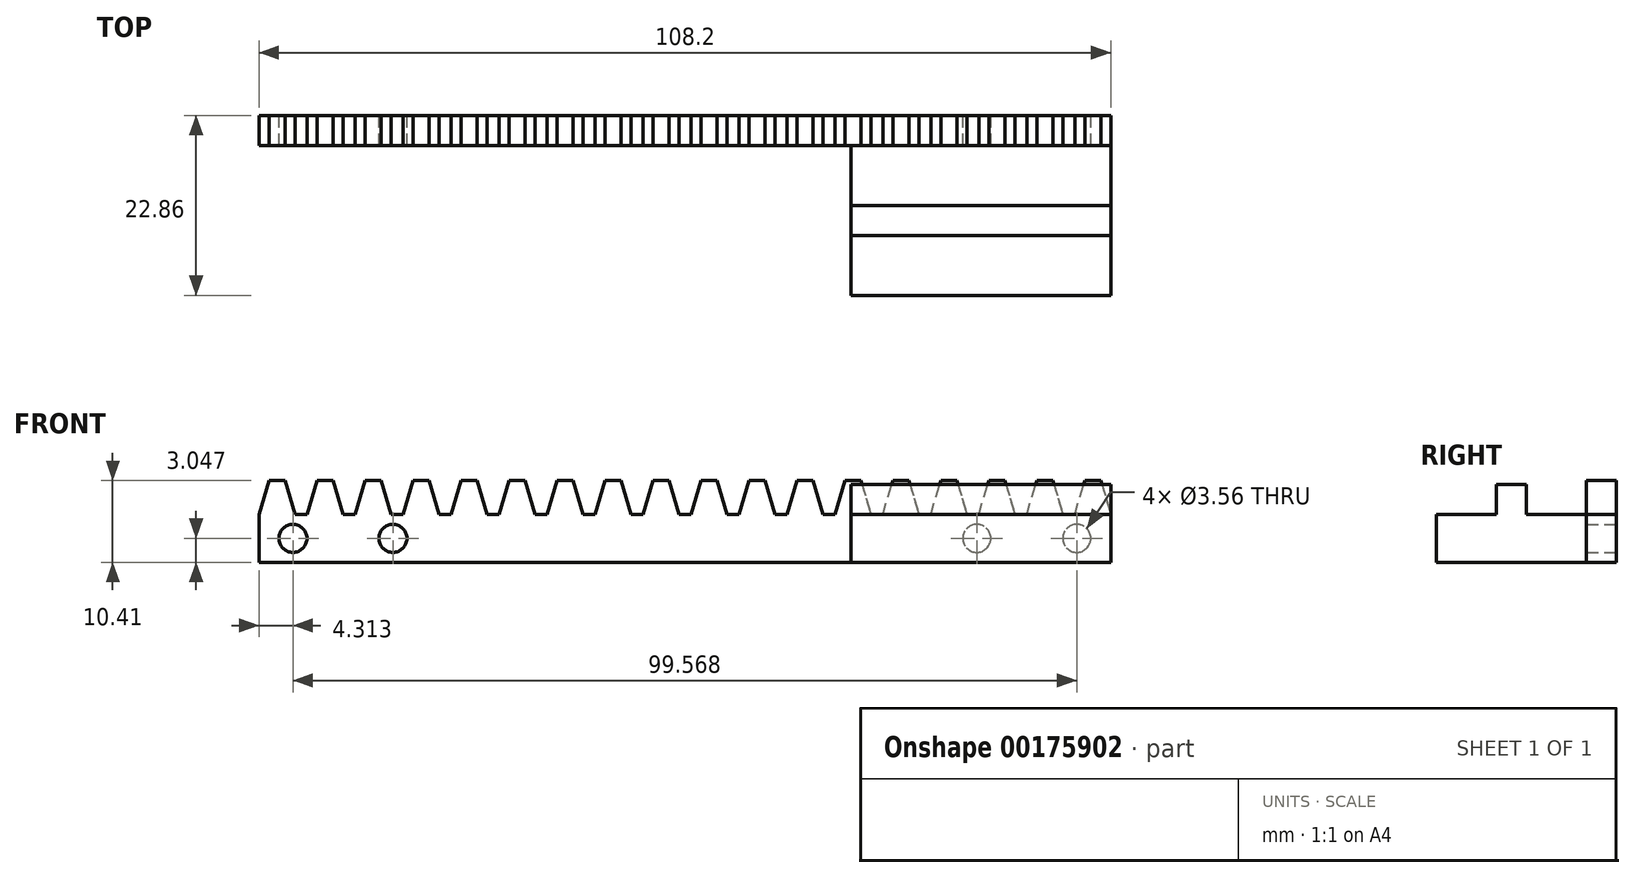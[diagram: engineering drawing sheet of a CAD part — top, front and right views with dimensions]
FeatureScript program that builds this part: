
annotation { "Feature Type Name" : "Feature", "Feature Type Description" : "" }
export const myFeature = defineFeature(function(context is Context, id is Id, definition is map)
    precondition{}
    {
        {
            var Q0;
            Q0=qCreatedBy(makeId("Front.planeOp"),FACE);
            var sketch = newSketch(context, id + "F0", { "sketchPlane" : qUnion([Q0])});
            skLineSegment(sketch, "E0.bottom", {"start": v(-38.44, 10.8) * mm, "end": v(69.76, 10.8) * mm});
            skLineSegment(sketch, "E0.top", {"start": v(-38.44, 16.9) * mm, "end": v(69.76, 16.9) * mm});
            skLineSegment(sketch, "E0.left", {"start": v(-38.44, 10.8) * mm, "end": v(-38.44, 16.9) * mm});
            skLineSegment(sketch, "E1", {"start": v(-38.44, 16.9) * mm, "end": v(-37.17, 21.21) * mm});
            skLineSegment(sketch, "E2", {"start": v(-37.17, 21.21) * mm, "end": v(-35.14, 21.21) * mm});
            skLineSegment(sketch, "E3", {"start": v(-35.14, 21.21) * mm, "end": v(-33.87, 16.9) * mm});
            skLineSegment(sketch, "E4", {"start": v(-38.44, 16.9) * mm, "end": v(-33.87, 16.9) * mm});
            skLineSegment(sketch, "E5", {"start": v(-36.16, 21.21) * mm, "end": v(-36.16, 16.9) * mm, "construction": true});
            skLineSegment(sketch, "E6", {"start": v(69.76, 10.8) * mm, "end": v(69.76, 16.9) * mm});
            skLineSegment(sketch, "E7.1.0.0", {"start": v(-29.05, 21.21) * mm, "end": v(-27.78, 16.9) * mm});
            skLineSegment(sketch, "E7.1.0.1", {"start": v(-32.35, 16.9) * mm, "end": v(-31.08, 21.21) * mm});
            skLineSegment(sketch, "E7.1.0.2", {"start": v(-31.08, 21.21) * mm, "end": v(-29.05, 21.21) * mm});
            skLineSegment(sketch, "E7.2.0.0", {"start": v(-22.95, 21.21) * mm, "end": v(-21.68, 16.9) * mm});
            skLineSegment(sketch, "E7.2.0.1", {"start": v(-26.25, 16.9) * mm, "end": v(-24.98, 21.21) * mm});
            skLineSegment(sketch, "E7.2.0.2", {"start": v(-24.98, 21.21) * mm, "end": v(-22.95, 21.21) * mm});
            skLineSegment(sketch, "E7.3.0.0", {"start": v(-16.85, 21.21) * mm, "end": v(-15.58, 16.9) * mm});
            skLineSegment(sketch, "E7.3.0.1", {"start": v(-20.16, 16.9) * mm, "end": v(-18.89, 21.21) * mm});
            skLineSegment(sketch, "E7.3.0.2", {"start": v(-18.89, 21.21) * mm, "end": v(-16.85, 21.21) * mm});
            skLineSegment(sketch, "E7.4.0.0", {"start": v(-10.76, 21.21) * mm, "end": v(-9.49, 16.9) * mm});
            skLineSegment(sketch, "E7.4.0.1", {"start": v(-14.06, 16.9) * mm, "end": v(-12.8, 21.21) * mm});
            skLineSegment(sketch, "E7.4.0.2", {"start": v(-12.8, 21.21) * mm, "end": v(-10.76, 21.21) * mm});
            skLineSegment(sketch, "E7.5.0.0", {"start": v(-4.66, 21.21) * mm, "end": v(-3.4, 16.9) * mm});
            skLineSegment(sketch, "E7.5.0.1", {"start": v(-7.96, 16.9) * mm, "end": v(-6.7, 21.21) * mm});
            skLineSegment(sketch, "E7.5.0.2", {"start": v(-6.7, 21.21) * mm, "end": v(-4.66, 21.21) * mm});
            skLineSegment(sketch, "E7.6.0.0", {"start": v(1.43, 21.21) * mm, "end": v(2.7, 16.9) * mm});
            skLineSegment(sketch, "E7.6.0.1", {"start": v(-1.87, 16.9) * mm, "end": v(-0.6, 21.21) * mm});
            skLineSegment(sketch, "E7.6.0.2", {"start": v(-0.6, 21.21) * mm, "end": v(1.43, 21.21) * mm});
            skLineSegment(sketch, "E7.7.0.0", {"start": v(7.53, 21.21) * mm, "end": v(8.8, 16.9) * mm});
            skLineSegment(sketch, "E7.7.0.1", {"start": v(4.23, 16.9) * mm, "end": v(5.5, 21.21) * mm});
            skLineSegment(sketch, "E7.7.0.2", {"start": v(5.5, 21.21) * mm, "end": v(7.53, 21.21) * mm});
            skLineSegment(sketch, "E7.8.0.0", {"start": v(13.63, 21.21) * mm, "end": v(14.9, 16.9) * mm});
            skLineSegment(sketch, "E7.8.0.1", {"start": v(10.32, 16.9) * mm, "end": v(11.6, 21.21) * mm});
            skLineSegment(sketch, "E7.8.0.2", {"start": v(11.6, 21.21) * mm, "end": v(13.63, 21.21) * mm});
            skLineSegment(sketch, "E7.9.0.0", {"start": v(19.72, 21.21) * mm, "end": v(21, 16.9) * mm});
            skLineSegment(sketch, "E7.9.0.1", {"start": v(16.42, 16.9) * mm, "end": v(17.69, 21.21) * mm});
            skLineSegment(sketch, "E7.9.0.2", {"start": v(17.69, 21.21) * mm, "end": v(19.72, 21.21) * mm});
            skLineSegment(sketch, "E7.10.0.0", {"start": v(25.82, 21.21) * mm, "end": v(27.09, 16.9) * mm});
            skLineSegment(sketch, "E7.10.0.1", {"start": v(22.52, 16.9) * mm, "end": v(23.79, 21.21) * mm});
            skLineSegment(sketch, "E7.10.0.2", {"start": v(23.79, 21.21) * mm, "end": v(25.82, 21.21) * mm});
            skLineSegment(sketch, "E7.11.0.0", {"start": v(31.91, 21.21) * mm, "end": v(33.18, 16.9) * mm});
            skLineSegment(sketch, "E7.11.0.1", {"start": v(28.61, 16.9) * mm, "end": v(29.88, 21.21) * mm});
            skLineSegment(sketch, "E7.11.0.2", {"start": v(29.88, 21.21) * mm, "end": v(31.91, 21.21) * mm});
            skLineSegment(sketch, "E7.12.0.0", {"start": v(38, 21.21) * mm, "end": v(39.28, 16.9) * mm});
            skLineSegment(sketch, "E7.12.0.1", {"start": v(34.7, 16.9) * mm, "end": v(35.98, 21.21) * mm});
            skLineSegment(sketch, "E7.12.0.2", {"start": v(35.98, 21.21) * mm, "end": v(38, 21.21) * mm});
            skLineSegment(sketch, "E7.13.0.0", {"start": v(44.1, 21.21) * mm, "end": v(45.38, 16.9) * mm});
            skLineSegment(sketch, "E7.13.0.1", {"start": v(40.8, 16.9) * mm, "end": v(42.07, 21.21) * mm});
            skLineSegment(sketch, "E7.13.0.2", {"start": v(42.07, 21.21) * mm, "end": v(44.1, 21.21) * mm});
            skLineSegment(sketch, "E7.14.0.0", {"start": v(50.2, 21.21) * mm, "end": v(51.47, 16.9) * mm});
            skLineSegment(sketch, "E7.14.0.1", {"start": v(46.9, 16.9) * mm, "end": v(48.17, 21.21) * mm});
            skLineSegment(sketch, "E7.14.0.2", {"start": v(48.17, 21.21) * mm, "end": v(50.2, 21.21) * mm});
            skLineSegment(sketch, "E7.15.0.0", {"start": v(56.3, 21.21) * mm, "end": v(57.57, 16.9) * mm});
            skLineSegment(sketch, "E7.15.0.1", {"start": v(53, 16.9) * mm, "end": v(54.27, 21.21) * mm});
            skLineSegment(sketch, "E7.15.0.2", {"start": v(54.27, 21.21) * mm, "end": v(56.3, 21.21) * mm});
            skLineSegment(sketch, "E7.16.0.0", {"start": v(62.4, 21.21) * mm, "end": v(63.66, 16.9) * mm});
            skLineSegment(sketch, "E7.16.0.1", {"start": v(59.1, 16.9) * mm, "end": v(60.36, 21.21) * mm});
            skLineSegment(sketch, "E7.16.0.2", {"start": v(60.36, 21.21) * mm, "end": v(62.4, 21.21) * mm});
            skLineSegment(sketch, "E7.17.0.0", {"start": v(68.49, 21.21) * mm, "end": v(69.76, 16.9) * mm});
            skLineSegment(sketch, "E7.17.0.1", {"start": v(65.19, 16.9) * mm, "end": v(66.46, 21.21) * mm});
            skLineSegment(sketch, "E7.17.0.2", {"start": v(66.46, 21.21) * mm, "end": v(68.49, 21.21) * mm});
            skLineSegment(sketch, "E7.direction1", {"start": v(-38.44, 16.9) * mm, "end": v(-32.35, 16.9) * mm, "construction": true});
            skPoint(sketch, "E8.centerSnap0", {"position": v(-38.44, 13.85) * mm});
            skSolve(sketch);
        }
        {
            var Q0;
            Q0=qSketchRegion(id+"F0",true);
            extrude(context, id + "F1", {"entities" : qUnion([Q0]), "depth" : 3.8 * mm});
        }
        {
            var Q0;
            Q0=makeQuery(id+"F1.opExtrude","CAP_FACE",FACE,{"disambiguationData":[OSD([sQuery(id+"F0.wireOp",EDGE,"E0.bottom"),sQuery(id+"F0.wireOp",EDGE,"E0.top"),sQuery(id+"F0.wireOp",EDGE,"E0.left"),sQuery(id+"F0.wireOp",EDGE,"E1"),sQuery(id+"F0.wireOp",EDGE,"E2"),sQuery(id+"F0.wireOp",EDGE,"E3"),sQuery(id+"F0.wireOp",EDGE,"E6"),sQuery(id+"F0.wireOp",EDGE,"E7.1.0.0"),sQuery(id+"F0.wireOp",EDGE,"E7.1.0.1"),sQuery(id+"F0.wireOp",EDGE,"E7.1.0.2"),sQuery(id+"F0.wireOp",EDGE,"E7.2.0.0"),sQuery(id+"F0.wireOp",EDGE,"E7.2.0.1"),sQuery(id+"F0.wireOp",EDGE,"E7.2.0.2"),sQuery(id+"F0.wireOp",EDGE,"E7.3.0.0"),sQuery(id+"F0.wireOp",EDGE,"E7.3.0.1"),sQuery(id+"F0.wireOp",EDGE,"E7.3.0.2"),sQuery(id+"F0.wireOp",EDGE,"E7.4.0.0"),sQuery(id+"F0.wireOp",EDGE,"E7.4.0.1"),sQuery(id+"F0.wireOp",EDGE,"E7.4.0.2"),sQuery(id+"F0.wireOp",EDGE,"E7.5.0.0"),sQuery(id+"F0.wireOp",EDGE,"E7.5.0.1"),sQuery(id+"F0.wireOp",EDGE,"E7.5.0.2"),sQuery(id+"F0.wireOp",EDGE,"E7.6.0.0"),sQuery(id+"F0.wireOp",EDGE,"E7.6.0.1"),sQuery(id+"F0.wireOp",EDGE,"E7.6.0.2"),sQuery(id+"F0.wireOp",EDGE,"E7.7.0.0"),sQuery(id+"F0.wireOp",EDGE,"E7.7.0.1"),sQuery(id+"F0.wireOp",EDGE,"E7.7.0.2"),sQuery(id+"F0.wireOp",EDGE,"E7.8.0.0"),sQuery(id+"F0.wireOp",EDGE,"E7.8.0.1"),sQuery(id+"F0.wireOp",EDGE,"E7.8.0.2"),sQuery(id+"F0.wireOp",EDGE,"E7.9.0.0"),sQuery(id+"F0.wireOp",EDGE,"E7.9.0.1"),sQuery(id+"F0.wireOp",EDGE,"E7.9.0.2"),sQuery(id+"F0.wireOp",EDGE,"E7.10.0.0"),sQuery(id+"F0.wireOp",EDGE,"E7.10.0.1"),sQuery(id+"F0.wireOp",EDGE,"E7.10.0.2"),sQuery(id+"F0.wireOp",EDGE,"E7.11.0.0"),sQuery(id+"F0.wireOp",EDGE,"E7.11.0.1"),sQuery(id+"F0.wireOp",EDGE,"E7.11.0.2"),sQuery(id+"F0.wireOp",EDGE,"E7.12.0.0"),sQuery(id+"F0.wireOp",EDGE,"E7.12.0.1"),sQuery(id+"F0.wireOp",EDGE,"E7.12.0.2"),sQuery(id+"F0.wireOp",EDGE,"E7.13.0.0"),sQuery(id+"F0.wireOp",EDGE,"E7.13.0.1"),sQuery(id+"F0.wireOp",EDGE,"E7.13.0.2"),sQuery(id+"F0.wireOp",EDGE,"E7.14.0.0"),sQuery(id+"F0.wireOp",EDGE,"E7.14.0.1"),sQuery(id+"F0.wireOp",EDGE,"E7.14.0.2"),sQuery(id+"F0.wireOp",EDGE,"E7.15.0.0"),sQuery(id+"F0.wireOp",EDGE,"E7.15.0.1"),sQuery(id+"F0.wireOp",EDGE,"E7.15.0.2"),sQuery(id+"F0.wireOp",EDGE,"E7.16.0.0"),sQuery(id+"F0.wireOp",EDGE,"E7.16.0.1"),sQuery(id+"F0.wireOp",EDGE,"E7.16.0.2"),sQuery(id+"F0.wireOp",EDGE,"E7.17.0.0"),sQuery(id+"F0.wireOp",EDGE,"E7.17.0.1"),sQuery(id+"F0.wireOp",EDGE,"E7.17.0.2")])],"isStart":true});
            var sketch = newSketch(context, id + "F2", { "sketchPlane" : qUnion([Q0])});
            skCircle(sketch, "E9", {"center": v(-52.74, 13.85) * mm, "radius": 1.78 * mm});
            skCircle(sketch, "E10", {"center": v(-65.44, 13.85) * mm, "radius": 1.78 * mm});
            skLineSegment(sketch, "E11", {"start": v(-65.19, 16.9) * mm, "end": v(-69.76, 16.9) * mm, "construction": true});
            skCircle(sketch, "E12", {"center": v(21.43, 13.85) * mm, "radius": 1.78 * mm});
            skCircle(sketch, "E13", {"center": v(34.13, 13.85) * mm, "radius": 1.78 * mm});
            skSolve(sketch);
        }
        {
            var Q0;
            Q0 = qSketchRegion(id + "F2", true);
            extrude(context, id + "F3", {"entities" : qUnion([Q0]), "operationType" : NewBodyOperationType.REMOVE, "endBound" : BoundingType.UP_TO_NEXT, "oppositeDirection" : true, "depth" : 25.4 * mm});
        }
        {
            var Q0;
            Q0=qCreatedBy(makeId("Right.planeOp"),FACE);
            var Q1;
            Q1=makeQuery(id+"F1.opExtrude","CAP_VERTEX",VERTEX,{"disambiguationData":[OSD([sQuery(id+"F0.wireOp",EDGE,"E0.bottom"),sQuery(id+"F0.wireOp",EDGE,"E6")])],"isStart":false});
            cPlane(context, id + "F4", {"entities" : qUnion([Q0, Q1]), "cplaneType" : CPlaneType.PLANE_POINT, "offset" : 25.4 * mm, "width" : 152.4 * mm, "height" : 152.4 * mm});
        }
        {
            var Q0;
            Q0=qCreatedBy(id+"F4.planeOp",FACE);
            var sketch = newSketch(context, id + "F5", { "sketchPlane" : qUnion([Q0])});
            skLineSegment(sketch, "E14.0", {"start": v(-3.81, 10.8) * mm, "end": v(-3.81, 16.9) * mm});
            skLineSegment(sketch, "E15", {"start": v(-22.86, 16.9) * mm, "end": v(-15.24, 16.9) * mm});
            skLineSegment(sketch, "E16", {"start": v(-11.43, 16.9) * mm, "end": v(-11.43, 20.7) * mm});
            skLineSegment(sketch, "E17", {"start": v(-11.43, 20.7) * mm, "end": v(-15.24, 20.7) * mm});
            skLineSegment(sketch, "E18", {"start": v(-15.24, 20.7) * mm, "end": v(-15.24, 16.9) * mm});
            skLineSegment(sketch, "E19.trimOffspring", {"start": v(-11.43, 16.9) * mm, "end": v(-3.81, 16.9) * mm});
            skLineSegment(sketch, "E20", {"start": v(-3.81, 10.8) * mm, "end": v(-22.86, 10.8) * mm});
            skLineSegment(sketch, "E21", {"start": v(-22.86, 10.8) * mm, "end": v(-22.86, 16.9) * mm});
            skSolve(sketch);
        }
        {
            var Q0;
            Q0 = qSketchRegion(id + "F5", true);
            extrude(context, id + "F6", {"entities" : qUnion([Q0]), "oppositeDirection" : true, "depth" : 33.02 * mm});
        }
    });
